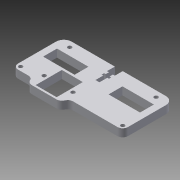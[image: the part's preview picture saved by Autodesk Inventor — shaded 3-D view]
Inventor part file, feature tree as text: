
AUTODESK INVENTOR PART (.ipt)
format: ipt  version: 2013 (Build 170138000, 138)  size: 137,728 bytes
history: native  units: mm
features: extrude x1, sketch x1
ambient origin geometry x8: Origin, YZ Plane, XZ Plane, XY Plane, X Axis, Y Axis, Z Axis, Center Point
bodies: Solid1 (feature_tree)
feature tree (2):
  extrude  "Extrusion1"  [1 undecoded]
  sketch  "Sketch1"  dims[d0=6.0mm d1=0.0mm]
note: 1 required parameter value undecoded (feature->parameter linkage not recoverable at this tier; creation-order binding heuristic only, values carry confidence <= 0.55)
